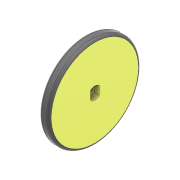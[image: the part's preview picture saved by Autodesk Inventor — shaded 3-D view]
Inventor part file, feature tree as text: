
AUTODESK INVENTOR PART (.ipt)
format: ipt  version: 2022 (Build 260153000, 153)  size: 140,288 bytes
history: native  units: mm
features: sketch x3, extrude x2, hole x1, fillet x1
ambient origin geometry x8: Origin, YZ Plane, XZ Plane, XY Plane, X Axis, Y Axis, Z Axis, Center Point
bodies: Solid1 (feature_tree)
feature tree (7):
  extrude  "Extrusion1"  Depth=4.0mm
  extrude  "Extrusion2"  Depth=3.5mm
  hole  "Hole1"  [1 undecoded]
  fillet  "Fillet1"  [1 undecoded]
  sketch  "Sketch1"  dims[d1=4.0mm d2=0.0mm d3=38.0mm]
  sketch  "Sketch2"  dims[d5=3.5mm d6=5.0mm]
  sketch  "Sketch3"  dims[d7=2.0mm d8=0.0mm d9=2.0mm d10=6.0mm d11=4.0mm d12=2.0mm d13=90.0deg d14=8.0mm d15=20.594885mm d16=1.0mm]
note: 2 required parameter values undecoded (feature->parameter linkage not recoverable at this tier; creation-order binding heuristic only, values carry confidence <= 0.55)
